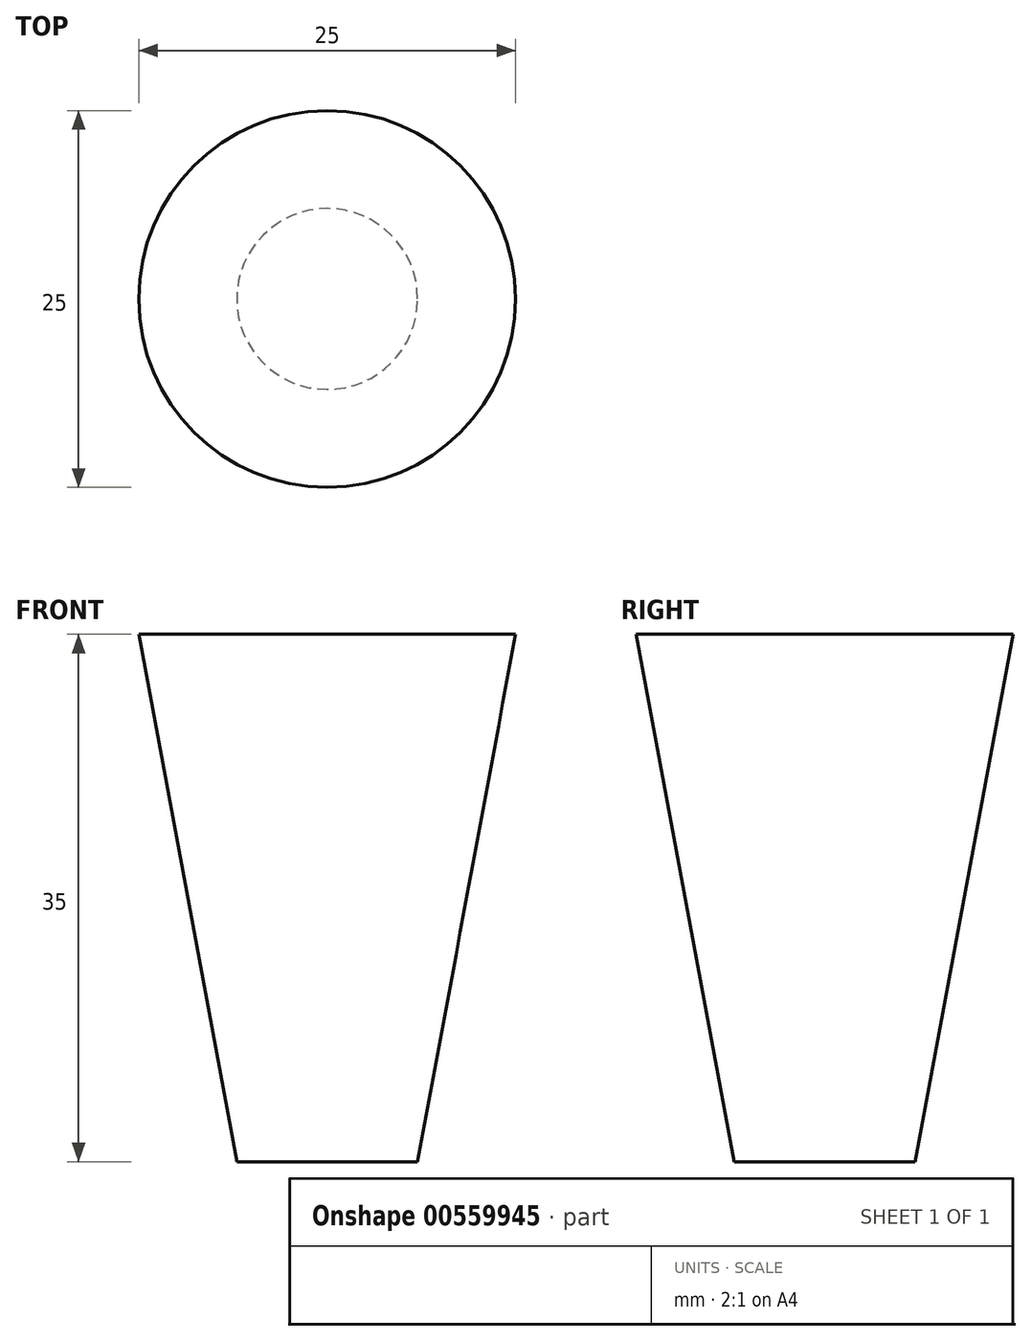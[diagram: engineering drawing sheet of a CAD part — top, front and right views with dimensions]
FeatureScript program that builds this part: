
annotation { "Feature Type Name" : "Feature", "Feature Type Description" : "" }
export const myFeature = defineFeature(function(context is Context, id is Id, definition is map)
    precondition{}
    {
        {
            var Q0;
            Q0=qCreatedBy(makeId("Top.planeOp"),FACE);
            var sketch = newSketch(context, id + "F0", { "sketchPlane" : qUnion([Q0])});
            skCircle(sketch, "E0", {"center": v(0, 0) * mm, "radius": 6 * mm});
            skSolve(sketch);
        }
        {
            var Q0;
            Q0=qCreatedBy(makeId("Front.planeOp"),FACE);
            var sketch = newSketch(context, id + "F1", { "sketchPlane" : qUnion([Q0])});
            skLineSegment(sketch, "E1", {"start": v(-4.58, 35) * mm, "end": v(20.42, 35) * mm});
            skSolve(sketch);
        }
        {
            var Q0;
            Q0=sQuery(id+"F1.wireOp",EDGE,"E1");
            cPlane(context, id + "F2", {"entities" : qUnion([Q0]), "cplaneType" : CPlaneType.LINE_ANGLE, "offset" : 25 * mm, "angle" : 90 * degree, "width" : 150 * mm, "height" : 150 * mm});
        }
        {
            var Q0;
            Q0=qCreatedBy(id+"F2.planeOp",FACE);
            var sketch = newSketch(context, id + "F3", { "sketchPlane" : qUnion([Q0])});
            skCircle(sketch, "E2", {"center": v(0, 0) * mm, "radius": 12.5 * mm});
            skSolve(sketch);
        }
        {
            var Q0;
            Q0=makeQuery(id+"F0.imprint","IMPRINT",FACE,{"disambiguationData":[TD([[makeQuery(id+"F0.imprint","IMPRINT",EDGE,{"derivedFrom":sQuery(id+"F0.wireOp",EDGE,"E0")}),1.0]])]});
            var Q1;
            Q1=makeQuery(id+"F3.imprint","IMPRINT",FACE,{"disambiguationData":[TD([[makeQuery(id+"F3.imprint","IMPRINT",EDGE,{"derivedFrom":sQuery(id+"F3.wireOp",EDGE,"E2")}),1.0]])]});
            loft(context, id + "F4", {"sheetProfilesArray" : [{ "sheetProfileEntities" : qUnion([Q0]) }, { "sheetProfileEntities" : qUnion([Q1]) }]});
        }
        {
            var Q0;
            Q0=qCreatedBy(makeId("Front.planeOp"),FACE);
            var sketch = newSketch(context, id + "F5", { "sketchPlane" : qUnion([Q0])});
            skLineSegment(sketch, "E3", {"start": v(0, 0) * mm, "end": v(0, 80) * mm, "construction": true});
            skLineSegment(sketch, "E4", {"start": v(0, 80) * mm, "end": v(15.23, 80) * mm, "construction": true});
            skSolve(sketch);
        }
        {
            var Q0;
            Q0=sQuery(id+"F5.wireOp",EDGE,"E4");
            cPlane(context, id + "F6", {"entities" : qUnion([Q0]), "cplaneType" : CPlaneType.LINE_ANGLE, "offset" : 25 * mm, "angle" : 90 * degree, "width" : 150 * mm, "height" : 150 * mm});
        }
    });
